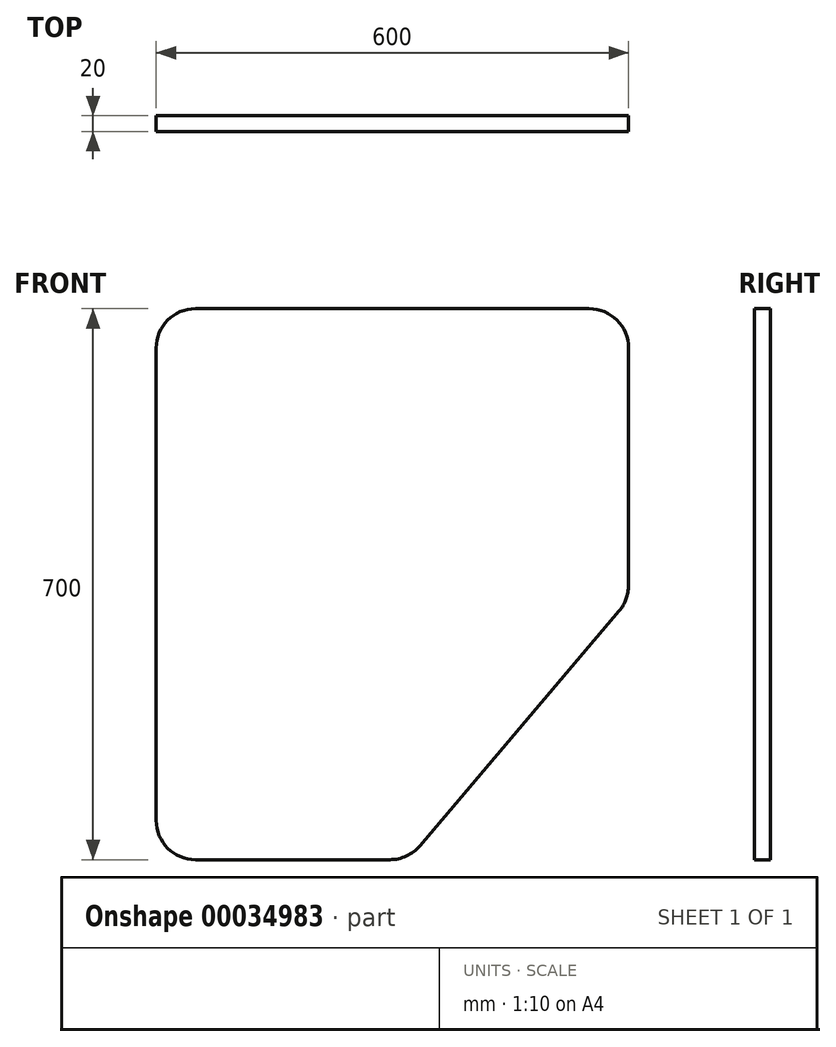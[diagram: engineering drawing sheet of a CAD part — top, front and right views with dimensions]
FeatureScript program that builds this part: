
annotation { "Feature Type Name" : "Feature", "Feature Type Description" : "" }
export const myFeature = defineFeature(function(context is Context, id is Id, definition is map)
    precondition{}
    {
        {
            var Q0;
            Q0=qCreatedBy(makeId("Front.planeOp"),FACE);
            var sketch = newSketch(context, id + "F0", { "sketchPlane" : qUnion([Q0])});
            skLineSegment(sketch, "E0", {"start": v(50, 0) * mm, "end": v(550, 0) * mm});
            skLineSegment(sketch, "E1", {"start": v(600, -50) * mm, "end": v(600, -351.65) * mm});
            skLineSegment(sketch, "E2", {"start": v(588.13, -384) * mm, "end": v(334.98, -682.35) * mm});
            skLineSegment(sketch, "E3", {"start": v(296.85, -700) * mm, "end": v(50, -700) * mm});
            skLineSegment(sketch, "E4", {"start": v(0, -650) * mm, "end": v(0, -50) * mm});
            skPoint(sketch, "E5.visualSharp", {"position": v(0, 0) * mm});
            skArc(sketch, "E5.filletArc", {"start": v(50, 0) * mm, "mid": v(14.64, -14.64) * mm, "end": v(0, -50) * mm});
            skPoint(sketch, "E6.visualSharp", {"position": v(600, 0) * mm});
            skArc(sketch, "E6.filletArc", {"start": v(600, -50) * mm, "mid": v(585.36, -14.64) * mm, "end": v(550, 0) * mm});
            skPoint(sketch, "E7.visualSharp", {"position": v(600, -370) * mm});
            skArc(sketch, "E7.filletArc", {"start": v(588.13, -384) * mm, "mid": v(596.94, -368.88) * mm, "end": v(600, -351.65) * mm});
            skPoint(sketch, "E8.visualSharp", {"position": v(320, -700) * mm});
            skArc(sketch, "E8.filletArc", {"start": v(296.85, -700) * mm, "mid": v(317.86, -695.37) * mm, "end": v(334.98, -682.35) * mm});
            skPoint(sketch, "E9.visualSharp", {"position": v(0, -700) * mm});
            skArc(sketch, "E9.filletArc", {"start": v(0, -650) * mm, "mid": v(14.64, -685.36) * mm, "end": v(50, -700) * mm});
            skSolve(sketch);
        }
        {
            var Q0;
            Q0=makeQuery(id+"F0.imprint","IMPRINT",FACE,{"disambiguationData":[TD([[makeQuery(id+"F0.imprint","IMPRINT",EDGE,{"derivedFrom":sQuery(id+"F0.wireOp",EDGE,"E0")}),-1.0]])]});
            extrude(context, id + "F1", {"entities" : qUnion([Q0]), "depth" : 20 * mm});
        }
    });
